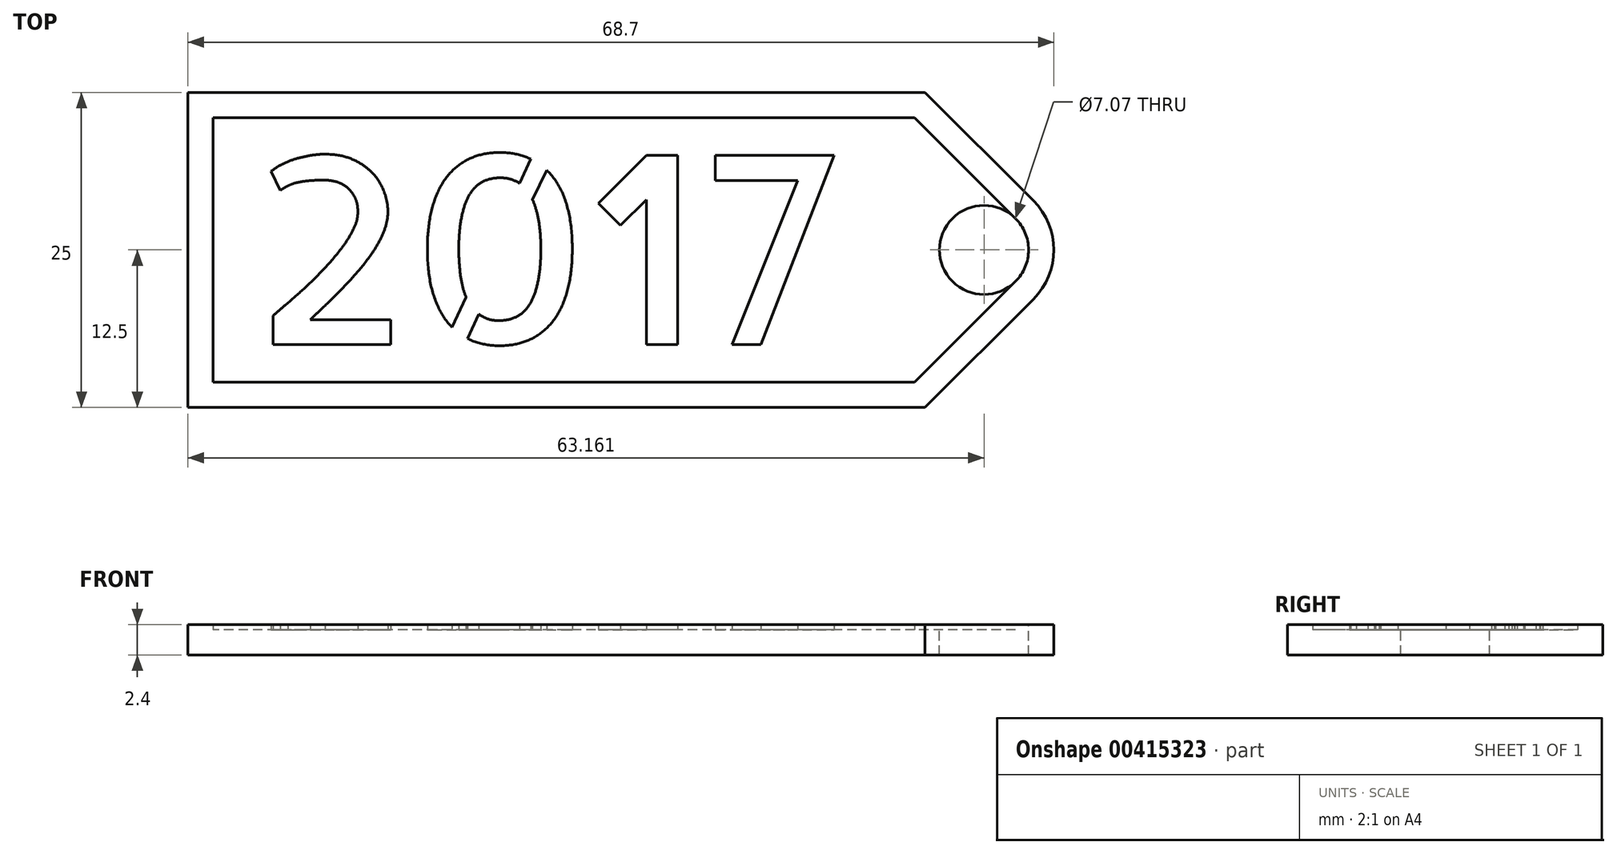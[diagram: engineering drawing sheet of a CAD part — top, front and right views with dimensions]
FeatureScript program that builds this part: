
annotation { "Feature Type Name" : "Feature", "Feature Type Description" : "" }
export const myFeature = defineFeature(function(context is Context, id is Id, definition is map)
    precondition{}
    {
        {
            var Q0;
            Q0=qCreatedBy(makeId("Top.planeOp"),FACE);
            var sketch = newSketch(context, id + "F0", { "sketchPlane" : qUnion([Q0])});
            skText(sketch, "E0", { "text": "2017", "fontName": "AllertaStencil-Regular.ttf"});
            skLineSegment(sketch, "E1", {"start": v(-26.83, 10.5) * mm, "end": v(-26.83, -10.5) * mm});
            skLineSegment(sketch, "E2", {"start": v(-26.83, -10.5) * mm, "end": v(28.83, -10.5) * mm});
            skLineSegment(sketch, "E3", {"start": v(36.83, -2.5) * mm, "end": v(28.83, -10.5) * mm});
            skLineSegment(sketch, "E4", {"start": v(36.83, -2.5) * mm, "end": v(36.83, 2.5) * mm, "construction": true});
            skLineSegment(sketch, "E5", {"start": v(36.83, 2.5) * mm, "end": v(28.83, 10.5) * mm});
            skLineSegment(sketch, "E6", {"start": v(28.83, 10.5) * mm, "end": v(-26.83, 10.5) * mm});
            skArc(sketch, "E7", {"start": v(36.83, 2.5) * mm, "mid": v(37.87, 0) * mm, "end": v(36.83, -2.5) * mm});
            skLineSegment(sketch, "E8.0", {"start": v(38.25, 3.91) * mm, "end": v(29.66, 12.5) * mm});
            skLineSegment(sketch, "E8.1", {"start": v(-28.83, 12.5) * mm, "end": v(-28.83, -12.5) * mm});
            skLineSegment(sketch, "E8.2", {"start": v(-28.83, -12.5) * mm, "end": v(29.66, -12.5) * mm});
            skLineSegment(sketch, "E8.3", {"start": v(29.66, 12.5) * mm, "end": v(-28.83, 12.5) * mm});
            skLineSegment(sketch, "E8.4", {"start": v(38.25, -3.91) * mm, "end": v(29.66, -12.5) * mm});
            skArc(sketch, "E8.5", {"start": v(38.25, 3.91) * mm, "mid": v(39.87, 0) * mm, "end": v(38.25, -3.91) * mm});
            skCircle(sketch, "E9", {"center": v(34.33, 0) * mm, "radius": 3.54 * mm});
            const initialGuessF0  = {"E0": [-0.02383, -0.0075, 1, 0, 0.015]};
            skSetInitialGuess(sketch, initialGuessF0);
            skSolve(sketch);
        }
        {
            var Q0;
            Q0=makeQuery(id+"F0.imprint","IMPRINT",FACE,{"disambiguationData":[TD([[makeQuery(id+"F0.imprint","IMPRINT",EDGE,{"derivedFrom":sQuery(id+"F0.wireOp",EDGE,"E1")}),-1.0]])]});
            var Q1;
            Q1=makeQuery(id+"F0.imprint","IMPRINT",FACE,{"disambiguationData":[TD([[makeQuery(id+"F0.imprint","IMPRINT",EDGE,{"derivedFrom":sQuery(id+"F0.wireOp",EDGE,"E0.sketch_text.stroke-0")}),1.0]])]});
            var Q2;
            Q2=makeQuery(id+"F0.imprint","IMPRINT",FACE,{"disambiguationData":[TD([[makeQuery(id+"F0.imprint","IMPRINT",EDGE,{"derivedFrom":sQuery(id+"F0.wireOp",EDGE,"E0.sketch_text.stroke-0")}),-1.0]])]});
            var Q3;
            Q3=makeQuery(id+"F0.imprint","IMPRINT",FACE,{"disambiguationData":[TD([[makeQuery(id+"F0.imprint","IMPRINT",EDGE,{"derivedFrom":sQuery(id+"F0.wireOp",EDGE,"E0.sketch_text.stroke-33")}),-1.0]])]});
            var Q4;
            Q4=makeQuery(id+"F0.imprint","IMPRINT",FACE,{"disambiguationData":[TD([[makeQuery(id+"F0.imprint","IMPRINT",EDGE,{"derivedFrom":sQuery(id+"F0.wireOp",EDGE,"E0.sketch_text.stroke-49")}),-1.0]])]});
            var Q5;
            Q5=makeQuery(id+"F0.imprint","IMPRINT",FACE,{"disambiguationData":[TD([[makeQuery(id+"F0.imprint","IMPRINT",EDGE,{"derivedFrom":sQuery(id+"F0.wireOp",EDGE,"E0.sketch_text.stroke-66")}),-1.0]])]});
            var Q6;
            Q6=makeQuery(id+"F0.imprint","IMPRINT",FACE,{"disambiguationData":[TD([[makeQuery(id+"F0.imprint","IMPRINT",EDGE,{"derivedFrom":sQuery(id+"F0.wireOp",EDGE,"E0.sketch_text.stroke-73")}),-1.0]])]});
            extrude(context, id + "F1", {"entities" : qUnion([Q0, Q1, Q2, Q3, Q4, Q5, Q6]), "oppositeDirection" : true, "depth" : 2 * mm});
        }
        {
            var Q0;
            Q0=makeQuery(id+"F0.imprint","IMPRINT",FACE,{"disambiguationData":[TD([[makeQuery(id+"F0.imprint","IMPRINT",EDGE,{"derivedFrom":sQuery(id+"F0.wireOp",EDGE,"E0.sketch_text.stroke-73")}),-1.0]])]});
            var Q1;
            Q1=makeQuery(id+"F0.imprint","IMPRINT",FACE,{"disambiguationData":[TD([[makeQuery(id+"F0.imprint","IMPRINT",EDGE,{"derivedFrom":sQuery(id+"F0.wireOp",EDGE,"E1")}),-1.0]])]});
            var Q2;
            Q2=makeQuery(id+"F0.imprint","IMPRINT",FACE,{"disambiguationData":[TD([[makeQuery(id+"F0.imprint","IMPRINT",EDGE,{"derivedFrom":sQuery(id+"F0.wireOp",EDGE,"E0.sketch_text.stroke-66")}),-1.0]])]});
            var Q3;
            Q3=makeQuery(id+"F0.imprint","IMPRINT",FACE,{"disambiguationData":[TD([[makeQuery(id+"F0.imprint","IMPRINT",EDGE,{"derivedFrom":sQuery(id+"F0.wireOp",EDGE,"E0.sketch_text.stroke-49")}),-1.0]])]});
            var Q4;
            Q4=makeQuery(id+"F0.imprint","IMPRINT",FACE,{"disambiguationData":[TD([[makeQuery(id+"F0.imprint","IMPRINT",EDGE,{"derivedFrom":sQuery(id+"F0.wireOp",EDGE,"E0.sketch_text.stroke-33")}),-1.0]])]});
            var Q5;
            Q5=makeQuery(id+"F0.imprint","IMPRINT",FACE,{"disambiguationData":[TD([[makeQuery(id+"F0.imprint","IMPRINT",EDGE,{"derivedFrom":sQuery(id+"F0.wireOp",EDGE,"E0.sketch_text.stroke-0")}),-1.0]])]});
            extrude(context, id + "F2", {"entities" : qUnion([Q0, Q1, Q2, Q3, Q4, Q5]), "operationType" : NewBodyOperationType.ADD, "depth" : 0.4 * mm});
        }
    });
